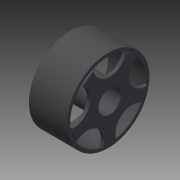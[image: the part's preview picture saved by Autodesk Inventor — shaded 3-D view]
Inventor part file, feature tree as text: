
AUTODESK INVENTOR PART (.ipt)
format: ipt  version: 2015 (Build 190159000, 159)  size: 136,192 bytes
history: native  units: in
note: dims shown in document units (in); Inventor stores cm internally (conversion verified against a paired STEP export)
features: sketch x3, extrude x3
ambient origin geometry x8: Origin, YZ Plane, XZ Plane, XY Plane, X Axis, Y Axis, Z Axis, Center Point
bodies: Solid1 (feature_tree)
feature tree (6):
  sketch  "Sketch1"  dims[d0=0.05in d1=0.44in]
  extrude  "Extrusion1"  Depth=0.05in
  sketch  "Sketch3"  dims[d2=0.05in d3=0.35in]
  extrude  "Extrusion2"  Depth=0.05in
  extrude  "Extrusion3"  Depth=0.05in TaperAngle=0.0deg
  sketch  "Sketch4"  dims[d4=0.57in d5=0.0in d6=0.05in d7=0.0in d8=0.5in d9=1.9685in d11=360.0deg d13=0.1in d14=0.0in]
